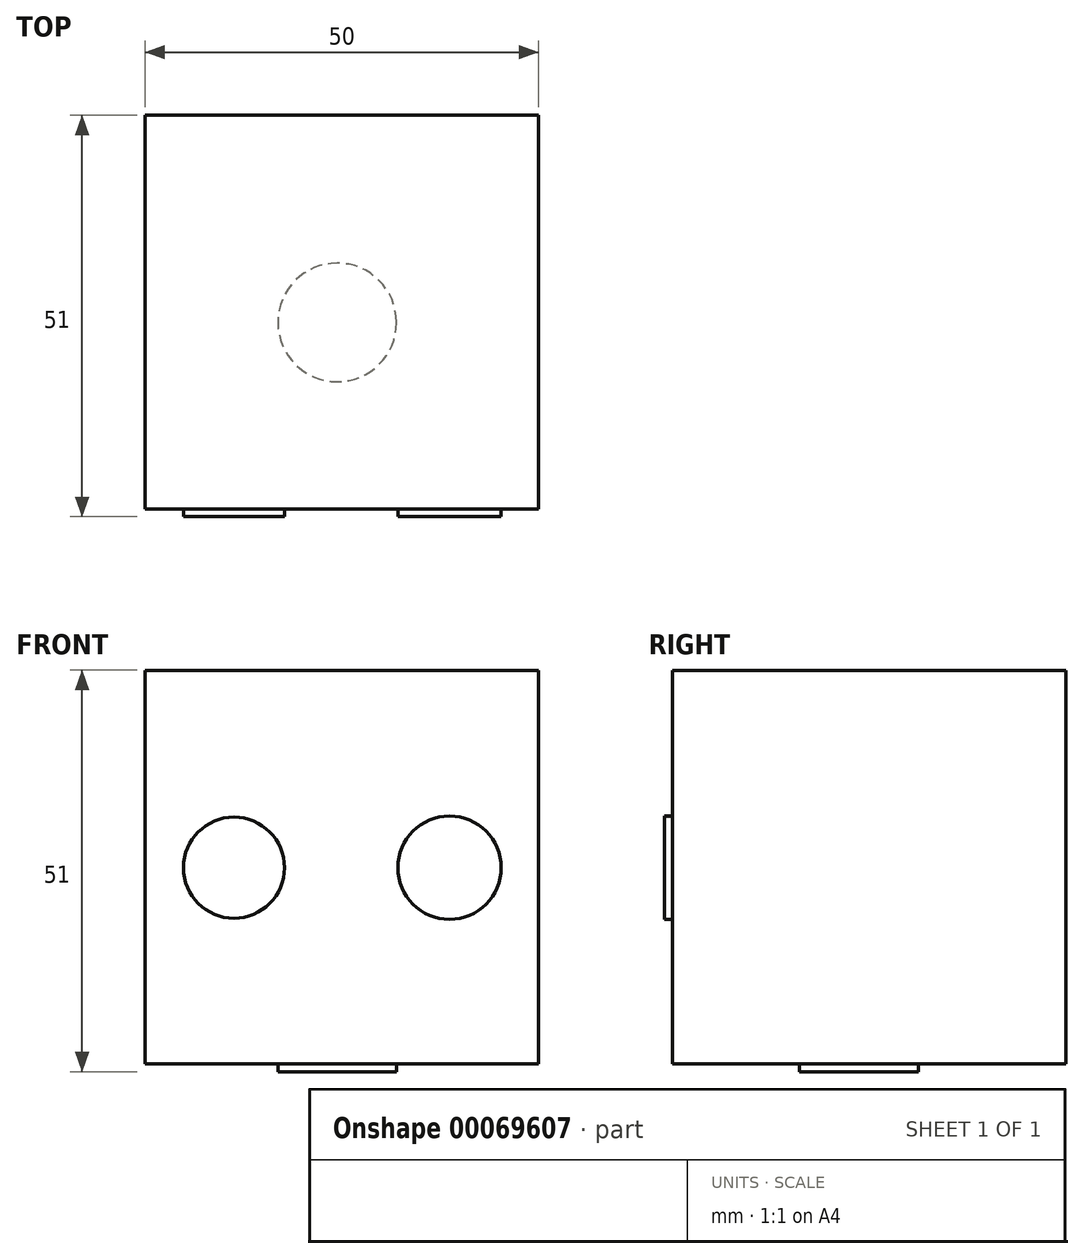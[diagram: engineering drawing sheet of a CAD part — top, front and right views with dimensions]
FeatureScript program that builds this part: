
annotation { "Feature Type Name" : "Feature", "Feature Type Description" : "" }
export const myFeature = defineFeature(function(context is Context, id is Id, definition is map)
    precondition{}
    {
        {
            var Q0;
            Q0=qCreatedBy(makeId("Front.planeOp"),FACE);
            var sketch = newSketch(context, id + "F0", { "sketchPlane" : qUnion([Q0])});
            skLineSegment(sketch, "E0.bottom", {"start": v(-24.41, 25.09) * mm, "end": v(25.59, 25.09) * mm});
            skLineSegment(sketch, "E0.top", {"start": v(-24.41, -24.91) * mm, "end": v(25.59, -24.91) * mm});
            skLineSegment(sketch, "E0.left", {"start": v(-24.41, 25.09) * mm, "end": v(-24.41, -24.91) * mm});
            skLineSegment(sketch, "E0.right", {"start": v(25.59, 25.09) * mm, "end": v(25.59, -24.91) * mm});
            skSolve(sketch);
        }
        {
            var Q0;
            Q0=makeQuery(id+"F0.imprint","IMPRINT",FACE,{"disambiguationData":[TD([[makeQuery(id+"F0.imprint","IMPRINT",EDGE,{"derivedFrom":sQuery(id+"F0.wireOp",EDGE,"E0.bottom")}),-1.0]])]});
            extrude(context, id + "F1", {"entities" : qUnion([Q0]), "depth" : 50 * mm});
        }
        {
            var Q0;
            Q0=makeQuery(id+"F1.opExtrude","SWEPT_FACE",FACE,{"disambiguationData":[OSD([sQuery(id+"F0.wireOp",EDGE,"E0.top")])]});
            var sketch = newSketch(context, id + "F2", { "sketchPlane" : qUnion([Q0])});
            skCircle(sketch, "E1", {"center": v(0, 26.31) * mm, "radius": 7.53 * mm});
            skSolve(sketch);
        }
        {
            var Q0;
            Q0 = qSketchRegion(id + "F2", true);
            extrude(context, id + "F3", {"entities" : qUnion([Q0]), "operationType" : NewBodyOperationType.ADD, "depth" : 1 * mm});
        }
        {
            var Q0;
            Q0=makeQuery(id+"F1.opExtrude","CAP_FACE",FACE,{"disambiguationData":[OSD([sQuery(id+"F0.wireOp",EDGE,"E0.bottom"),sQuery(id+"F0.wireOp",EDGE,"E0.top"),sQuery(id+"F0.wireOp",EDGE,"E0.left"),sQuery(id+"F0.wireOp",EDGE,"E0.right")])],"isStart":false});
            var sketch = newSketch(context, id + "F4", { "sketchPlane" : qUnion([Q0])});
            skCircle(sketch, "E2", {"center": v(-13.1, 0) * mm, "radius": 6.42 * mm});
            skCircle(sketch, "E3", {"center": v(14.27, 0) * mm, "radius": 6.57 * mm});
            skSolve(sketch);
        }
        {
            var Q0;
            Q0=makeQuery(id+"F4.imprint","IMPRINT",FACE,{"disambiguationData":[TD([[makeQuery(id+"F4.imprint","IMPRINT",EDGE,{"derivedFrom":sQuery(id+"F4.wireOp",EDGE,"E2")}),1.0]])]});
            var Q1;
            Q1=makeQuery(id+"F4.imprint","IMPRINT",FACE,{"disambiguationData":[TD([[makeQuery(id+"F4.imprint","IMPRINT",EDGE,{"derivedFrom":sQuery(id+"F4.wireOp",EDGE,"E3")}),1.0]])]});
            extrude(context, id + "F5", {"entities" : qUnion([Q0, Q1]), "operationType" : NewBodyOperationType.ADD, "depth" : 1 * mm});
        }
    });
